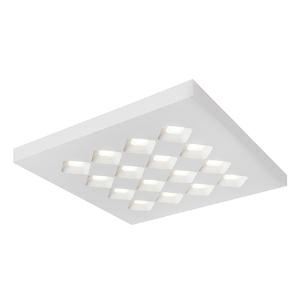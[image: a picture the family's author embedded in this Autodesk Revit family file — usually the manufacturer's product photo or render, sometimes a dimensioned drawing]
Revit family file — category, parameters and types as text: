
# Revit family: 3f_filippi_-_3f_diagon_p_soft_ugr_3f_filippi_-_12134_-_3f_diagon_p_39w-930_soft_ugr_596x596
name_source: partatom
category: Lighting Fixtures
units: mm (PartAtom-declared; Revit-internal decimal feet)

## family parameters
Cut with Voids When Loaded = No
Host = Face
Light Source = No
Part Type = Normal
Room Calculation Point = No
Round Connector Dimension = Use Diameter
Shared = No

## types (1)
- 3F Filippi - 3F Dìagon P Soft UGR (1 x LED, 3664 lm, 40 W, 3000 K)
    Apparent Load = 40 VA
    Approval mark = CE
    CIE Flux Codes = 59 92 100 100 100
    Color Rendering = 90
    Color Temperature = 3000 K
    Control Gear = Electronic ballast
    Default Elevation = 1800 mm
    Description = ILLUMINOTECHNICAL
Luminous efficiency 100% (DLOR 100%, ULOR 0%).
Initial luminous flux of the luminaire 3664 lm.
Direct symmetric distribution.
Installation Interdistance Transv.D = 1.23 x hu - Long.D = 1.23 x hu.
Average luminance <3000 cd/m² for radial angles >65°.
Tabular UGR (CIE 117 - 4H-8H; S=0.25H; 70/50/20): RUG 18.7 - 18.7.
Beam angle: 102° - 101°.
Luminous efficacy 92 lm/W.
Lifetime (L90/B10): 30000 h. (tq+25°C)
Lifetime (L85/B10): 50000 h. (tq+25°C)
Lifetime (L80/B20): 80000 h. (tq+25°C)
Lifetime (L70/B20): 100000 h. (tq+25°C)
Sudden decreased luminous flux after 50000 hours: 0% (C0).
Photobiological safety in compliance with IEC/TR 62778: RG0 risk exempt, (IEC 62471).
In compliance with IEC/EN 62722-2-1 - IEC/EN 62717 standards.

SOURCE
Squared LED module 39W/930.
Energy efficiency class (UE 2019/2020 - UE 2019/2015): E.
CIE 13.3 Colour rendering index: CRI >90 (R9 >50%).
IES TM-30 Fidelity Index: Rf = 92 Rg = 101.
CCT nominal colour temperature 3000 K.
Colour initial tolerance (MacAdam): SDCM 3.

MECHANICAL
White painted frame.
Height only 40 mm.
Housing in hot-galvanised steel, painted in white polyester.
Honeycombed diagonal screen in white anti-glare polycarbonate.
Opal methacrylate (PMMA) rhomboid lenses with differentiated, engraved and prismatic surfaces for diffused, soft lighting and excellent visual comfort.
Luminaire with limited surface temperature. - D - (EN 60598-2-24)
Dimensions: 596x596 mm, height 40 mm. Weight 6.2 kg.
IP40 protection degree.
Mechanical strength to impacts IK06 (1 joule).
Glow-wire test resistance 650°C.

ELECTRICAL
Halogen Free electronic wiring 230V-50/60Hz, power factor 0.90, THD <25%, constant output current, class I, 1 driver.
Power of the luminaire 40 W.
ENEC - CE.
SAFE FLICKER: PstLM=<1 and SVM=<0.4 (IEC TR 61547-1 and IEC TR 63158), to ensure a more comfortable and safe light.
Luminaire compliant with EN 60598-2-22 for power supply from a centralised emergency system CPSS (Central Power Supply System), not incorporated in the luminaire - high risk areas excluded. The default power and flux are 100% in AC and 100% in DC.
Ambient temperature from 0°C to +25°C.
Temperature class T6 max 85°C.
Quick connection.
Relative humidity UR: <85%.

INSTALLATION
Ceiling.

APPLICATIONS
Environments: staterooms, with VDTs, offices.
Environments with exacting visual tasks, where diffused soft light for optimum visual comfort is required.

WARNING
Luminaire designed for disposal/recycling at end-of-life.
Replaceable (LED only) light source by a professional. Replaceable control gear by a professional.
    Height = 40 mm  [stored 0.131234 ft]
    Lamp = 1 x LED
    Lamp Light Flux = 3664 lm
    Lamp Power = 40 W
    Lamp count = 1
    Length = 596 mm
    Lifetime = 50000 h
    Luminous efficacy = 92 lm/W
    Manufacturer = 3F Filippi
    ModVariant = No
    Model = 3F Filippi - 12134 - 3F Diagon P 39W-930 SOFT UGR 596x596
    Mounting Place = Ceiling
    Mounting Type = Surface mounted
    Number of Poles = 1
    OnlyDefault = Yes
    Power Factor = 1
    Product Name = 3F Filippi - 3F Dìagon P Soft UGR
    Product group = ceiling mounted luminaire
    ProductGroupID = 3
    Protection Class = Protection class I
    Protection Degree = IP 40
    RLX_Detail_Level = 1
    RLX_Emergency_Light_Flux = 0 lm
    RLX_Emergency_Type = 0
    RLX_Emergency_Type_DB = No
    RlxData = <blob elided: 94845 chars, md5=34b8992e>
    Socket = socket
    Standby Power = 0 W
    System Light Flux = 3664 lm
    System Power = 40 W
    Type Comments = Product without accessories
    Type Image = 3ffilippi_3f_diagon_p_soft_ugr.jpg
    URL = http://relux.com
    VarID = ---
    Voltage = 0 V
    Weight = 0.00 kg
    Width = 596 mm

note: [stored X ft] marks values corroborated as IEEE doubles in the binary element streams (Revit-internal decimal feet)

## geometry (parser evidence)
native form markers: Blend x4, Sweep x10
no freeform markers — native parametric forms only
